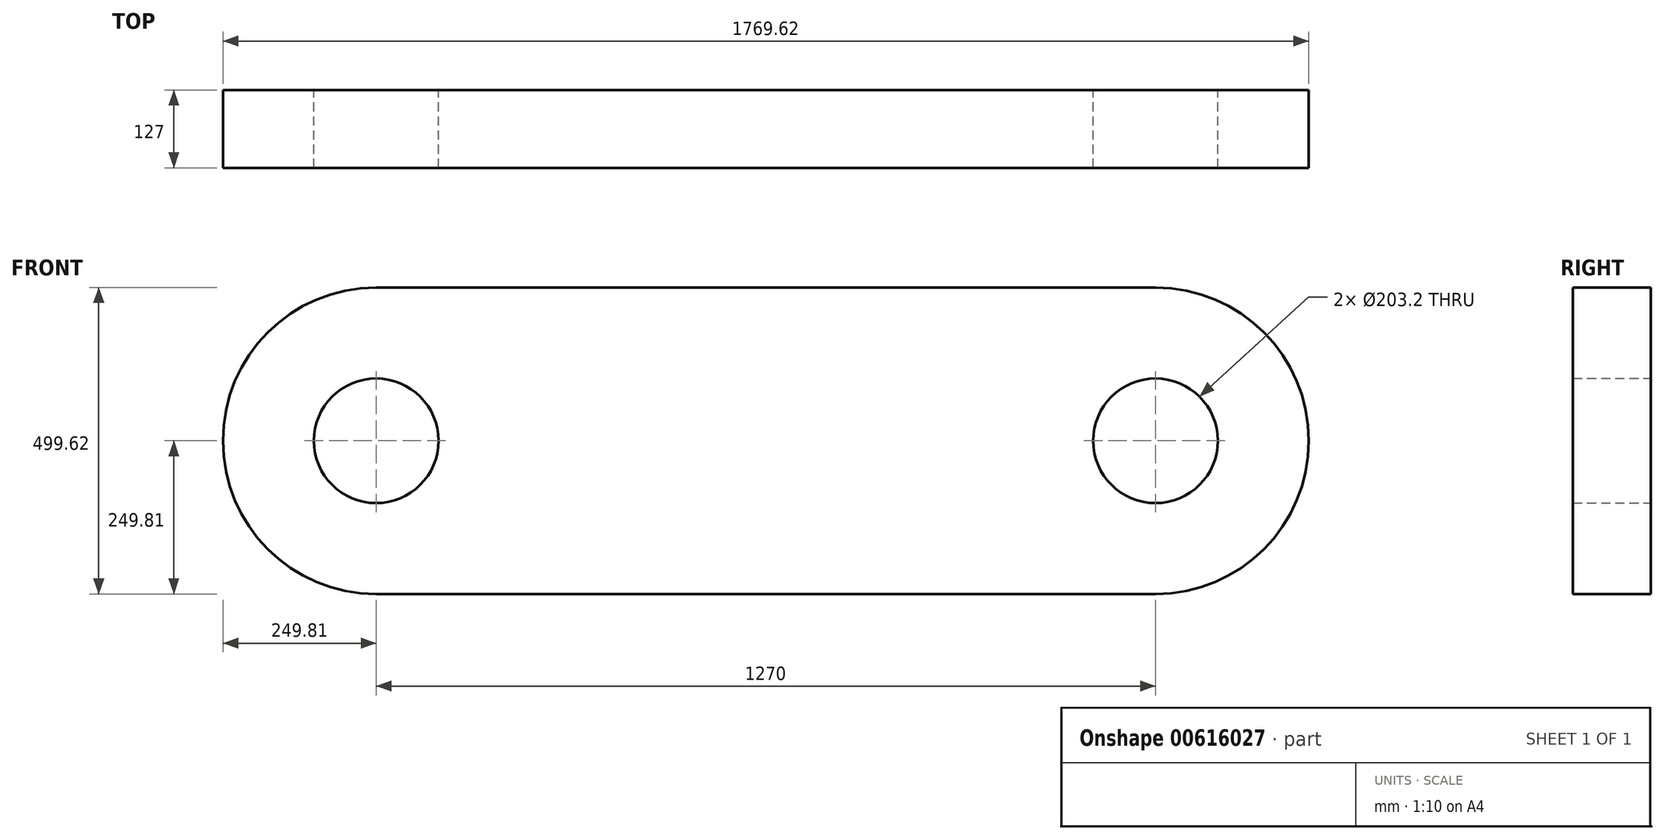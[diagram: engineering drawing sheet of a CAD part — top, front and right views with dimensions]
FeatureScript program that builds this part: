
annotation { "Feature Type Name" : "Feature", "Feature Type Description" : "" }
export const myFeature = defineFeature(function(context is Context, id is Id, definition is map)
    precondition{}
    {
        {
            var Q0;
            Q0=qCreatedBy(makeId("Front.planeOp"),FACE);
            var sketch = newSketch(context, id + "F0", { "sketchPlane" : qUnion([Q0])});
            skLineSegment(sketch, "E0", {"start": v(-635, 0) * mm, "end": v(635, 0) * mm});
            skCircle(sketch, "E1", {"center": v(-635, 0) * mm, "radius": 249.8 * mm});
            skCircle(sketch, "E2", {"center": v(635, 0) * mm, "radius": 249.8 * mm});
            skCircle(sketch, "E3", {"center": v(-635, 0) * mm, "radius": 101.6 * mm});
            skCircle(sketch, "E4", {"center": v(635, 0) * mm, "radius": 101.6 * mm});
            skLineSegment(sketch, "E5", {"start": v(-635, 249.8) * mm, "end": v(635, 249.8) * mm});
            skLineSegment(sketch, "E6", {"start": v(635, -249.8) * mm, "end": v(-635, -249.8) * mm});
            skSolve(sketch);
        }
        {
            var Q0;
            Q0 = qSketchRegion(id + "F0", true);
            extrude(context, id + "F1", {"entities" : qUnion([Q0]), "depth" : 127 * mm, "offsetDistance" : 25.4 * mm});
        }
    });
